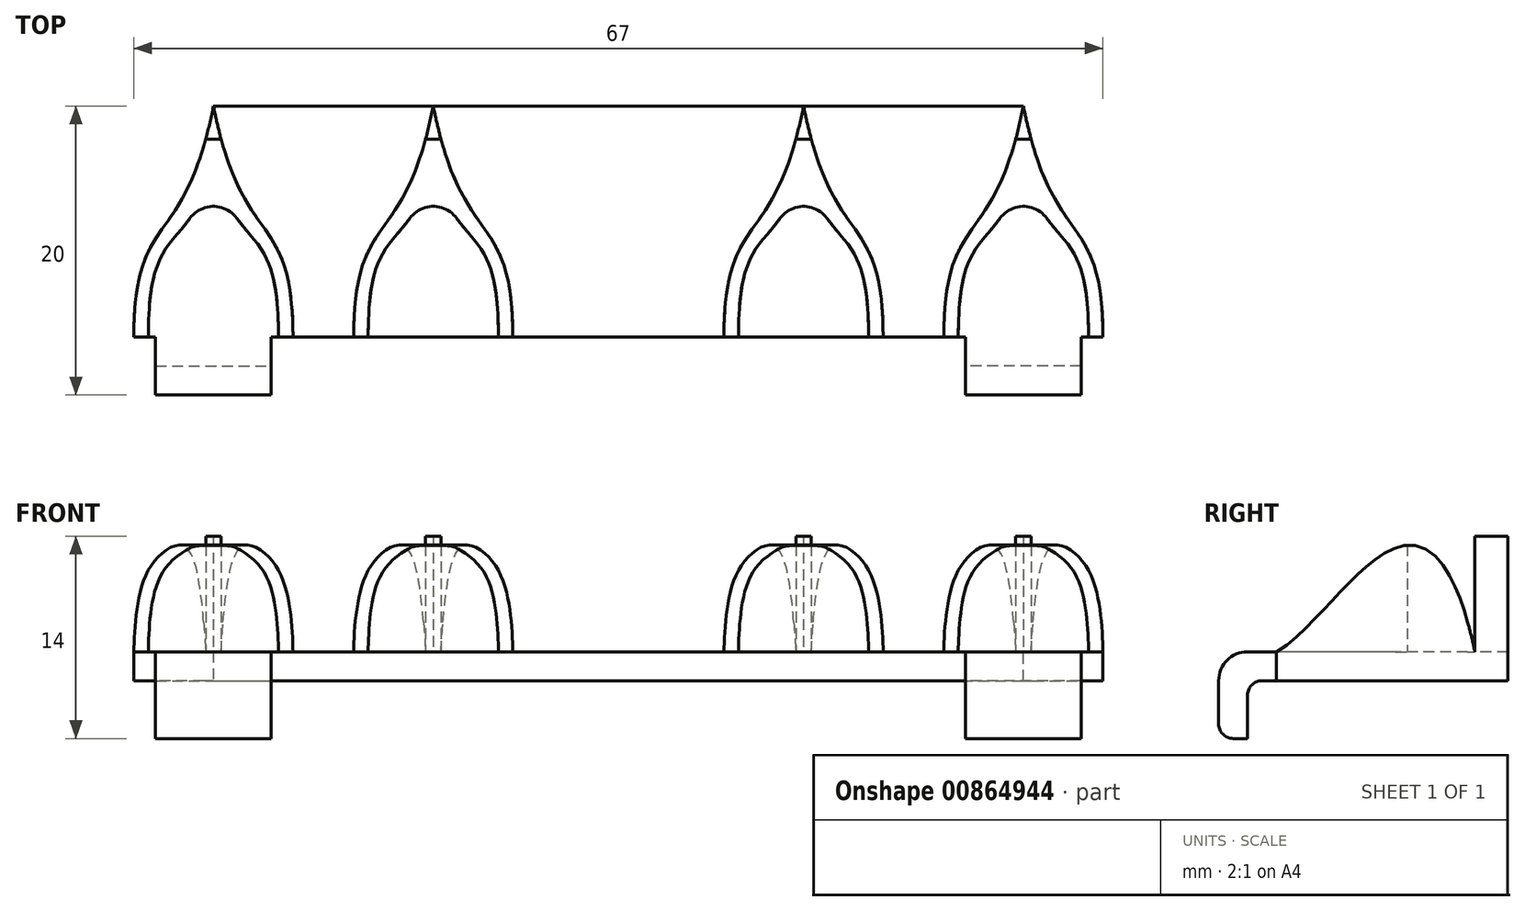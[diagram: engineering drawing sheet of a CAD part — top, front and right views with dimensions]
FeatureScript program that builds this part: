
annotation { "Feature Type Name" : "Feature", "Feature Type Description" : "" }
export const myFeature = defineFeature(function(context is Context, id is Id, definition is map)
    precondition{}
    {
        {
            var Q0;
            Q0=qCreatedBy(makeId("Top.planeOp"),FACE);
            var sketch = newSketch(context, id + "F0", { "sketchPlane" : qUnion([Q0])});
            skLineSegment(sketch, "E0.bottom", {"start": v(-29, 15) * mm, "end": v(29, 15) * mm, "construction": true});
            skLineSegment(sketch, "E0.top", {"start": v(-29, -15) * mm, "end": v(29, -15) * mm, "construction": true});
            skLineSegment(sketch, "E0.left", {"start": v(-29, 15) * mm, "end": v(-29, -15) * mm, "construction": true});
            skLineSegment(sketch, "E0.right", {"start": v(29, 15) * mm, "end": v(29, -15) * mm, "construction": true});
            skPoint(sketch, "E0.middle", {"position": v(0, 0) * mm});
            skLineSegment(sketch, "E1", {"start": v(-28, -15) * mm, "end": v(-28, 1) * mm, "construction": true});
            skLineSegment(sketch, "E2", {"start": v(-28, -15) * mm, "end": v(-33.5, -15) * mm, "construction": true});
            skLineSegment(sketch, "E3", {"start": v(-28, -15) * mm, "end": v(-22.5, -15) * mm, "construction": true});
            skFitSpline(sketch, "E4", {"points": [v(-28, 1) * mm, v(-33.5, -15) * mm], "startDerivative": vector(-6, -30.55) * mm, "endDerivative": vector(0, -27) * mm});
            skLineSegment(sketch, "E5", {"start": v(-33.5, -15) * mm, "end": v(-33.5, -6) * mm, "construction": true});
            skLineSegment(sketch, "E6", {"start": v(-22.5, -15) * mm, "end": v(-22.5, -6) * mm, "construction": true});
            skFitSpline(sketch, "E7", {"points": [v(-28, 1) * mm, v(-22.5, -15) * mm], "startDerivative": vector(6, -30.55) * mm, "endDerivative": vector(0, -27) * mm});
            skLineSegment(sketch, "E8", {"start": v(-28, -9.18) * mm, "end": v(-30, -9.18) * mm, "construction": true});
            skLineSegment(sketch, "E9", {"start": v(-28, -9.18) * mm, "end": v(-26, -9.18) * mm, "construction": true});
            skLineSegment(sketch, "E10", {"start": v(-28, 1) * mm, "end": v(0, 1) * mm, "construction": true});
            skLineSegment(sketch, "E11", {"start": v(-28, -15) * mm, "end": v(0, -15) * mm, "construction": true});
            skLineSegment(sketch, "E12", {"start": v(-28, 1) * mm, "end": v(-28, -3.5) * mm, "construction": true});
            skLineSegment(sketch, "E13", {"start": v(-22.5, -15) * mm, "end": v(-23.5, -15) * mm, "construction": true});
            skFitSpline(sketch, "E14", {"points": [v(-28, -3.5) * mm, v(-23.5, -15) * mm], "startDerivative": vector(6, -17.77) * mm, "endDerivative": vector(0, -24) * mm});
            skFitSpline(sketch, "E15.MirrorCS", {"points": [v(-28, -3.5) * mm, v(-32.5, -15) * mm], "startDerivative": vector(-6, -17.77) * mm, "endDerivative": vector(0, -24) * mm});
            skLineSegment(sketch, "E16", {"start": v(-33.5, -15) * mm, "end": v(-32.5, -15) * mm});
            skLineSegment(sketch, "E17", {"start": v(-23.5, -15) * mm, "end": v(-22.5, -15) * mm});
            skLineSegment(sketch, "E18.MirrorCS", {"start": v(33.5, -15) * mm, "end": v(32.5, -15) * mm});
            skLineSegment(sketch, "E19.MirrorCS", {"start": v(23.5, -15) * mm, "end": v(22.5, -15) * mm});
            skFitSpline(sketch, "E20.MirrorCS", {"points": [v(28, 1) * mm, v(33.5, -15) * mm], "startDerivative": vector(6, -30.55) * mm, "endDerivative": vector(0, -27) * mm});
            skFitSpline(sketch, "E21.MirrorCS", {"points": [v(28, -3.5) * mm, v(32.5, -15) * mm], "startDerivative": vector(6, -17.77) * mm, "endDerivative": vector(0, -24) * mm});
            skFitSpline(sketch, "E22.MirrorCS", {"points": [v(28, -3.5) * mm, v(23.5, -15) * mm], "startDerivative": vector(-6, -17.77) * mm, "endDerivative": vector(0, -24) * mm});
            skFitSpline(sketch, "E23.MirrorCS", {"points": [v(28, 1) * mm, v(22.5, -15) * mm], "startDerivative": vector(-6, -30.55) * mm, "endDerivative": vector(0, -27) * mm});
            skLineSegment(sketch, "E24", {"start": v(-22.5, -15) * mm, "end": v(-18.3, -15) * mm, "construction": true});
            skLineSegment(sketch, "E25", {"start": v(22.5, -15) * mm, "end": v(18.3, -15) * mm, "construction": true});
            skLineSegment(sketch, "E26", {"start": v(-20.4, -15) * mm, "end": v(-20.4, 3.77) * mm, "construction": true});
            skLineSegment(sketch, "E27.MirrorCS", {"start": v(-7.3, -15) * mm, "end": v(-8.3, -15) * mm});
            skLineSegment(sketch, "E28.MirrorCS", {"start": v(-17.3, -15) * mm, "end": v(-18.3, -15) * mm});
            skFitSpline(sketch, "E29.MirrorCS", {"points": [v(-12.8, 1) * mm, v(-7.3, -15) * mm], "startDerivative": vector(6, -30.55) * mm, "endDerivative": vector(0, -27) * mm});
            skFitSpline(sketch, "E30.MirrorCS", {"points": [v(-12.8, -3.5) * mm, v(-8.3, -15) * mm], "startDerivative": vector(6, -17.77) * mm, "endDerivative": vector(0, -24) * mm});
            skFitSpline(sketch, "E31.MirrorCS", {"points": [v(-12.8, -3.5) * mm, v(-17.3, -15) * mm], "startDerivative": vector(-6, -17.77) * mm, "endDerivative": vector(0, -24) * mm});
            skFitSpline(sketch, "E32.MirrorCS", {"points": [v(-12.8, 1) * mm, v(-18.3, -15) * mm], "startDerivative": vector(-6, -30.55) * mm, "endDerivative": vector(0, -27) * mm});
            skLineSegment(sketch, "E33.MirrorCS", {"start": v(7.3, -15) * mm, "end": v(8.3, -15) * mm});
            skLineSegment(sketch, "E34.MirrorCS", {"start": v(17.3, -15) * mm, "end": v(18.3, -15) * mm});
            skFitSpline(sketch, "E35.MirrorCS", {"points": [v(12.8, 1) * mm, v(18.3, -15) * mm], "startDerivative": vector(6, -30.55) * mm, "endDerivative": vector(0, -27) * mm});
            skFitSpline(sketch, "E36.MirrorCS", {"points": [v(12.8, -3.5) * mm, v(17.3, -15) * mm], "startDerivative": vector(6, -17.77) * mm, "endDerivative": vector(0, -24) * mm});
            skFitSpline(sketch, "E37.MirrorCS", {"points": [v(12.8, -3.5) * mm, v(8.3, -15) * mm], "startDerivative": vector(-6, -17.77) * mm, "endDerivative": vector(0, -24) * mm});
            skFitSpline(sketch, "E38.MirrorCS", {"points": [v(12.8, 1) * mm, v(7.3, -15) * mm], "startDerivative": vector(-6, -30.55) * mm, "endDerivative": vector(0, -27) * mm});
            skLineSegment(sketch, "E39", {"start": v(0, -6.7) * mm, "end": v(-7, -6.7) * mm, "construction": true});
            skLineSegment(sketch, "E40", {"start": v(-28, -9.42) * mm, "end": v(-30, -9.42) * mm, "construction": true});
            skLineSegment(sketch, "E41", {"start": v(-23.5, -15) * mm, "end": v(-23.5, -7) * mm, "construction": true});
            skLineSegment(sketch, "E42", {"start": v(-32.5, -15) * mm, "end": v(-32.5, -7) * mm, "construction": true});
            skArc(sketch, "E43.filletArc", {"start": v(-27.33, -1.79) * mm, "mid": v(-28, -1.28) * mm, "end": v(-28.67, -1.79) * mm});
            skArc(sketch, "E44.filletArc", {"start": v(-12.13, -1.79) * mm, "mid": v(-12.8, -1.28) * mm, "end": v(-13.47, -1.79) * mm});
            skArc(sketch, "E45.filletArc", {"start": v(13.47, -1.79) * mm, "mid": v(12.8, -1.28) * mm, "end": v(12.13, -1.79) * mm});
            skArc(sketch, "E46.filletArc", {"start": v(28.67, -1.79) * mm, "mid": v(28, -1.28) * mm, "end": v(27.33, -1.79) * mm});
            skSolve(sketch);
        }
        {
            var Q0;
            Q0 = qSketchRegion(id + "F0", true);
            extrude(context, id + "F1", {"entities" : qUnion([Q0]), "depth" : 8 * mm, "offsetDistance" : 25 * mm});
        }
        {
            var Q0;
            Q0=qCreatedBy(makeId("Right.planeOp"),FACE);
            var sketch = newSketch(context, id + "F2", { "sketchPlane" : qUnion([Q0])});
            skFitSpline(sketch, "E47", {"points": [v(-1.28, 0) * mm, v(-15, 0) * mm], "startDerivative": vector(-10.02, 46.49) * mm, "endDerivative": vector(-12.2, -6.26) * mm});
            skLineSegment(sketch, "E48", {"start": v(-15, 0) * mm, "end": v(-15, 12.12) * mm});
            skLineSegment(sketch, "E49", {"start": v(-15, 12.12) * mm, "end": v(-1.28, 12.12) * mm});
            skLineSegment(sketch, "E50", {"start": v(-1.28, 12.12) * mm, "end": v(-1.28, 0) * mm});
            skSolve(sketch);
        }
        {
            var Q0;
            Q0 = qSketchRegion(id + "F2", true);
            extrude(context, id + "F3", {"entities" : qUnion([Q0]), "operationType" : NewBodyOperationType.REMOVE, "oppositeDirection" : true, "depth" : 40 * mm, "offsetDistance" : 25 * mm, "hasSecondDirection" : true, "secondDirectionOppositeDirection" : false, "secondDirectionDepth" : 40 * mm});
        }
        {
            var Q0;
            Q0 = qSketchRegion(id + "F0", true);
            extrude(context, id + "F4", {"entities" : qUnion([Q0]), "oppositeDirection" : true, "depth" : 2 * mm, "offsetDistance" : 25 * mm});
        }
        {
            var Q0;
            Q0=makeQuery(id+"F4.opExtrude","SWEPT_FACE",FACE,{"disambiguationData":[OSD([sQuery(id+"F0.wireOp",EDGE,"E4")])]});
            var Q1;
            Q1=makeQuery(id+"F4.opExtrude","SWEPT_FACE",FACE,{"disambiguationData":[OSD([sQuery(id+"F0.wireOp",EDGE,"E20.MirrorCS")])]});
            loft(context, id + "F5", {"sheetProfilesArray" : [{ "sheetProfileEntities" : qUnion([Q0]) }, { "sheetProfileEntities" : qUnion([Q1]) }]});
        }
        {
            var Q0;
            Q0=qCreatedBy(makeId("Top.planeOp"),FACE);
            var sketch = newSketch(context, id + "F6", { "sketchPlane" : qUnion([Q0])});
            skLineSegment(sketch, "E51.bottom", {"start": v(28, -1.28) * mm, "end": v(-28, -1.28) * mm});
            skLineSegment(sketch, "E51.top", {"start": v(28, -1.98) * mm, "end": v(-28, -1.98) * mm});
            skLineSegment(sketch, "E51.left", {"start": v(28, -1.28) * mm, "end": v(28, -1.98) * mm});
            skLineSegment(sketch, "E51.right", {"start": v(-28, -1.28) * mm, "end": v(-28, -1.98) * mm});
            skSolve(sketch);
        }
        {
            var Q0;
            Q0 = qSketchRegion(id + "F6", true);
            extrude(context, id + "F7", {"entities" : qUnion([Q0]), "operationType" : NewBodyOperationType.ADD, "oppositeDirection" : true, "depth" : 2 * mm, "offsetDistance" : 25 * mm});
        }
        {
            var Q0;
            Q0=makeQuery(id+"F1.opExtrude","SWEPT_EDGE",EDGE,{"disambiguationData":[OSD([sQuery(id+"F0.wireOp",EDGE,"E36.MirrorCS"),sQuery(id+"F0.wireOp",EDGE,"E37.MirrorCS")])]});
            var Q1;
            Q1=makeQuery(id+"F1.opExtrude","SWEPT_EDGE",EDGE,{"disambiguationData":[OSD([sQuery(id+"F0.wireOp",EDGE,"E21.MirrorCS"),sQuery(id+"F0.wireOp",EDGE,"E22.MirrorCS")])]});
            var Q2;
            Q2=makeQuery(id+"F1.opExtrude","SWEPT_EDGE",EDGE,{"disambiguationData":[OSD([sQuery(id+"F0.wireOp",EDGE,"E30.MirrorCS"),sQuery(id+"F0.wireOp",EDGE,"E31.MirrorCS")])]});
            var Q3;
            Q3=makeQuery(id+"F1.opExtrude","SWEPT_EDGE",EDGE,{"disambiguationData":[OSD([sQuery(id+"F0.wireOp",EDGE,"E14"),sQuery(id+"F0.wireOp",EDGE,"E15.MirrorCS")])]});
            fillet(context, id + "F8", {"entities" : qUnion([Q0, Q1, Q2, Q3]), "radius" : 2 * mm, "tangentPropagation" : true, "allowEdgeOverflow" : false});
        }
        {
            var Q0;
            Q0=qCreatedBy(makeId("Right.planeOp"),FACE);
            var sketch = newSketch(context, id + "F9", { "sketchPlane" : qUnion([Q0])});
            skLineSegment(sketch, "E52", {"start": v(-15, -2) * mm, "end": v(-15, 0) * mm});
            skLineSegment(sketch, "E53", {"start": v(-15, -2) * mm, "end": v(-16, -2) * mm});
            skLineSegment(sketch, "E54", {"start": v(-17, -3) * mm, "end": v(-17, -6) * mm});
            skLineSegment(sketch, "E55", {"start": v(-17, -6) * mm, "end": v(-18, -6) * mm});
            skLineSegment(sketch, "E56", {"start": v(-19, -5) * mm, "end": v(-19, -2) * mm});
            skLineSegment(sketch, "E57", {"start": v(-17, 0) * mm, "end": v(-15, 0) * mm});
            skLineSegment(sketch, "E58", {"start": v(-38.66, 27.48) * mm, "end": v(-49.27, 27.48) * mm, "construction": true});
            skLineSegment(sketch, "E59", {"start": v(-49.27, 27.48) * mm, "end": v(-49.27, 22.03) * mm, "construction": true});
            skPoint(sketch, "E60.visualSharp", {"position": v(-17, -2) * mm});
            skArc(sketch, "E60.filletArc", {"start": v(-16, -2) * mm, "mid": v(-16.7, -2.3) * mm, "end": v(-17, -3) * mm});
            skPoint(sketch, "E61.visualSharp", {"position": v(-19, -6) * mm});
            skArc(sketch, "E61.filletArc", {"start": v(-19, -5) * mm, "mid": v(-18.7, -5.7) * mm, "end": v(-18, -6) * mm});
            skPoint(sketch, "E62.visualSharp", {"position": v(-19, 0) * mm});
            skArc(sketch, "E62.filletArc", {"start": v(-17, 0) * mm, "mid": v(-18.41, -0.59) * mm, "end": v(-19, -2) * mm});
            skSolve(sketch);
        }
        {
            var Q0;
            Q0 = qSketchRegion(id + "F9", true);
            extrude(context, id + "F10", {"entities" : qUnion([Q0]), "operationType" : NewBodyOperationType.ADD, "depth" : 32 * mm, "offsetDistance" : 25 * mm, "hasSecondDirection" : true, "secondDirectionOppositeDirection" : false, "secondDirectionDepth" : 24 * mm});
        }
        {
            var Q0;
            Q0 = qSketchRegion(id + "F9", true);
            extrude(context, id + "F11", {"entities" : qUnion([Q0]), "operationType" : NewBodyOperationType.ADD, "oppositeDirection" : true, "depth" : 32 * mm, "offsetDistance" : 25 * mm, "hasSecondDirection" : true, "secondDirectionOppositeDirection" : true, "secondDirectionDepth" : 24 * mm});
        }
    });
